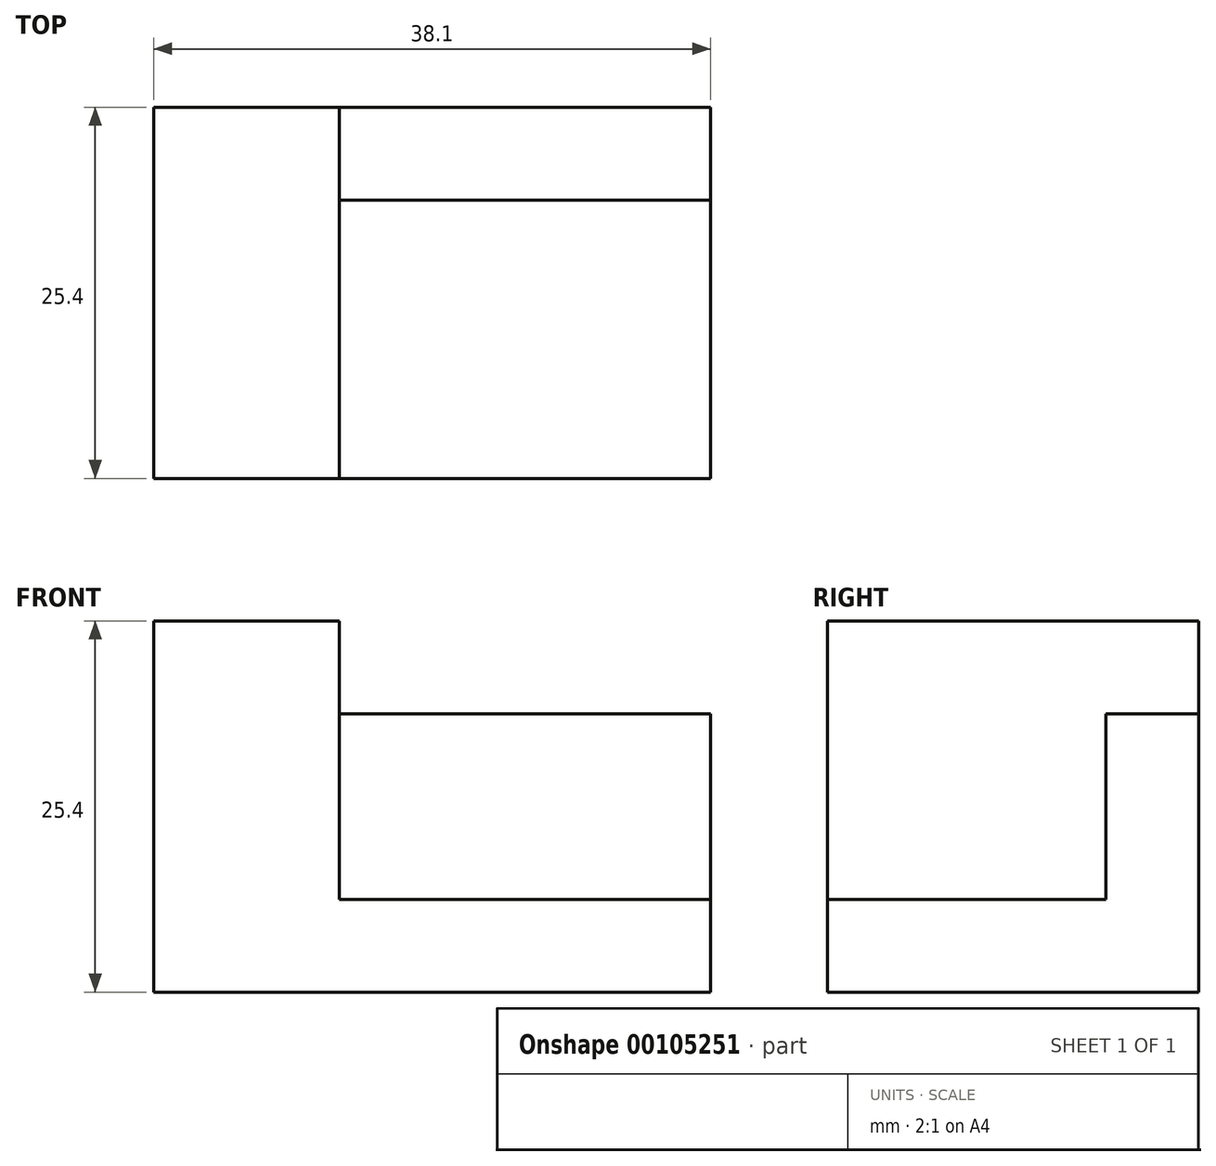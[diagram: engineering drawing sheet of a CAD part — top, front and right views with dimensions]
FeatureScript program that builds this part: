
annotation { "Feature Type Name" : "Feature", "Feature Type Description" : "" }
export const myFeature = defineFeature(function(context is Context, id is Id, definition is map)
    precondition{}
    {
        {
            var Q0;
            Q0=qCreatedBy(makeId("Right.planeOp"),FACE);
            var sketch = newSketch(context, id + "F0", { "sketchPlane" : qUnion([Q0])});
            skLineSegment(sketch, "E0", {"start": v(0, 0) * mm, "end": v(0, 6.35) * mm});
            skLineSegment(sketch, "E1", {"start": v(0, 6.35) * mm, "end": v(19.05, 6.35) * mm});
            skLineSegment(sketch, "E2", {"start": v(19.05, 6.35) * mm, "end": v(19.05, 19.05) * mm});
            skLineSegment(sketch, "E3", {"start": v(19.05, 19.05) * mm, "end": v(25.4, 19.05) * mm});
            skLineSegment(sketch, "E4", {"start": v(25.4, 19.05) * mm, "end": v(25.4, 0) * mm});
            skLineSegment(sketch, "E5", {"start": v(25.4, 0) * mm, "end": v(0, 0) * mm});
            skSolve(sketch);
        }
        {
            var Q0;
            Q0=makeQuery(id+"F0.imprint","IMPRINT",FACE,{"disambiguationData":[TD([[makeQuery(id+"F0.imprint","IMPRINT",EDGE,{"derivedFrom":sQuery(id+"F0.wireOp",EDGE,"E0")}),-1.0]])]});
            extrude(context, id + "F1", {"entities" : qUnion([Q0]), "depth" : 25.4 * mm});
        }
        {
            var Q0;
            Q0=makeQuery(id+"F1.opExtrude","CAP_FACE",FACE,{"disambiguationData":[OSD([sQuery(id+"F0.wireOp",EDGE,"E0"),sQuery(id+"F0.wireOp",EDGE,"E1"),sQuery(id+"F0.wireOp",EDGE,"E2"),sQuery(id+"F0.wireOp",EDGE,"E3"),sQuery(id+"F0.wireOp",EDGE,"E4"),sQuery(id+"F0.wireOp",EDGE,"E5")])],"isStart":true});
            var sketch = newSketch(context, id + "F2", { "sketchPlane" : qUnion([Q0])});
            skLineSegment(sketch, "E6.bottom", {"start": v(-25.4, 0) * mm, "end": v(0, 0) * mm});
            skLineSegment(sketch, "E6.top", {"start": v(-25.4, 25.4) * mm, "end": v(0, 25.4) * mm});
            skLineSegment(sketch, "E6.left", {"start": v(-25.4, 0) * mm, "end": v(-25.4, 25.4) * mm});
            skLineSegment(sketch, "E6.right", {"start": v(0, 0) * mm, "end": v(0, 25.4) * mm});
            skSolve(sketch);
        }
        {
            var Q0;
            Q0 = qSketchRegion(id + "F2", true);
            extrude(context, id + "F3", {"entities" : qUnion([Q0]), "operationType" : NewBodyOperationType.ADD, "depth" : 12.7 * mm});
        }
    });
